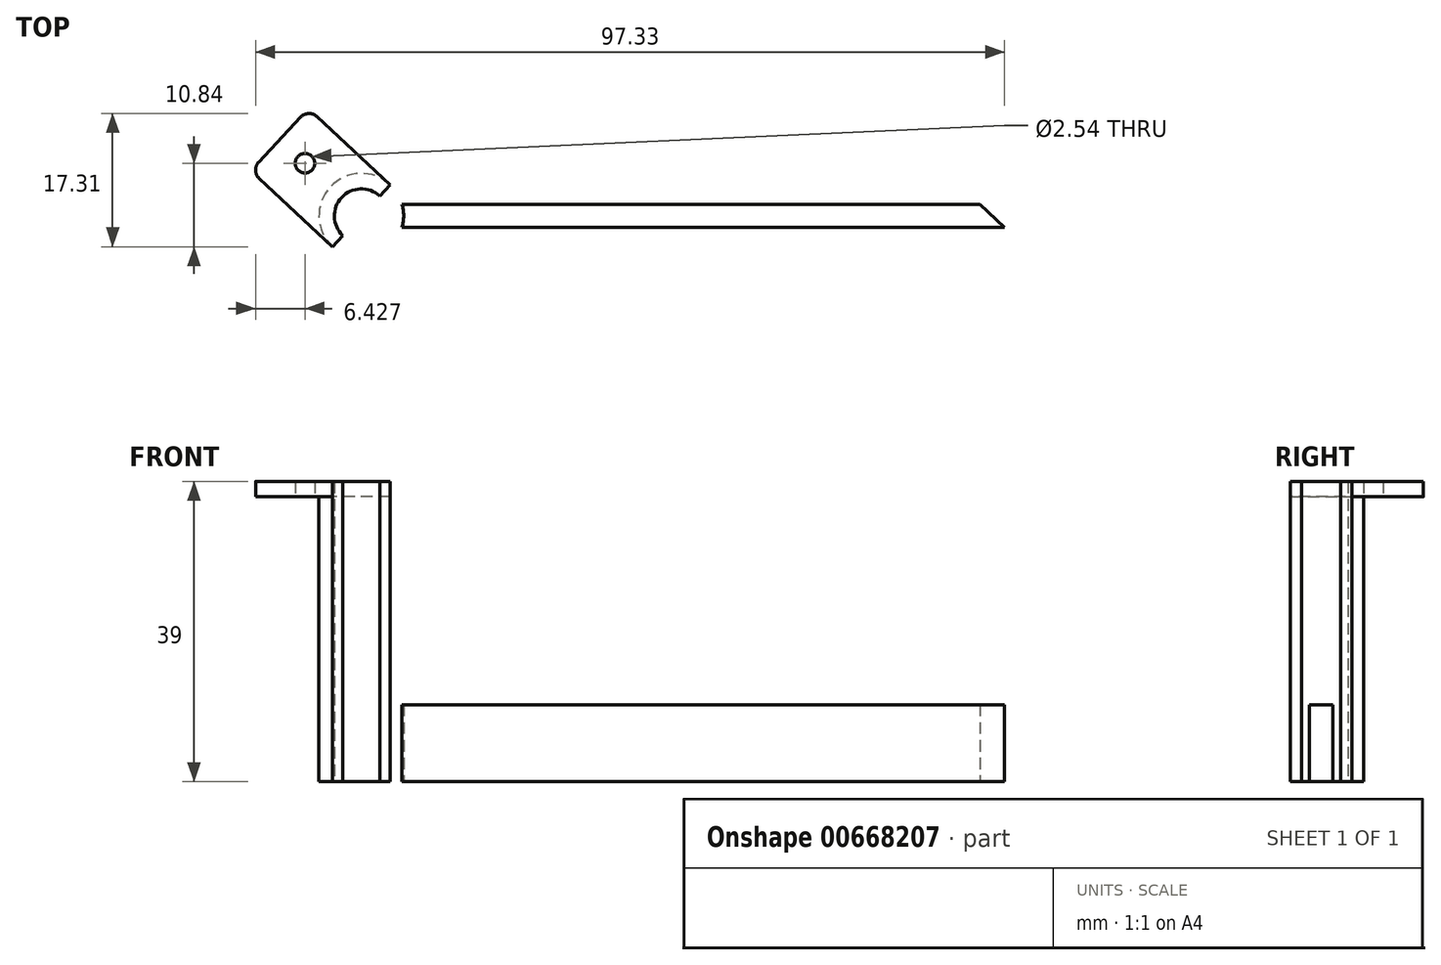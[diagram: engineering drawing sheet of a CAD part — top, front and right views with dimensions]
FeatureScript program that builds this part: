
annotation { "Feature Type Name" : "Feature", "Feature Type Description" : "" }
export const myFeature = defineFeature(function(context is Context, id is Id, definition is map)
    precondition{}
    {
        {
            var Q0;
            Q0=qCreatedBy(makeId("Top.planeOp"),FACE);
            var sketch = newSketch(context, id + "F0", { "sketchPlane" : qUnion([Q0])});
            skCircle(sketch, "E0", {"center": v(-44.5, 0) * mm, "radius": 3.5 * mm});
            skCircle(sketch, "E1", {"center": v(-44.5, 0) * mm, "radius": 5.5 * mm});
            skLineSegment(sketch, "E2", {"start": v(-39.2, 1.5) * mm, "end": v(35.87, 1.5) * mm});
            skLineSegment(sketch, "E3.MirrorCS", {"start": v(-39.2, -1.5) * mm, "end": v(39.1, -1.5) * mm});
            skPoint(sketch, "E4.orphan", {"position": v(39.1, -1.5) * mm});
            skLineSegment(sketch, "E5.bottom", {"start": v(-40.75, 4.02) * mm, "end": v(-48.25, -4.02) * mm});
            skLineSegment(sketch, "E5.top", {"start": v(-52.38, 12.81) * mm, "end": v(-57.83, 6.96) * mm});
            skLineSegment(sketch, "E5.left", {"start": v(-40.75, 4.02) * mm, "end": v(-50.26, 12.89) * mm});
            skLineSegment(sketch, "E5.right", {"start": v(-48.25, -4.02) * mm, "end": v(-57.76, 4.84) * mm});
            skPoint(sketch, "E6", {"position": v(-48.25, -4.02) * mm});
            skCircle(sketch, "E7", {"center": v(-51.81, 6.82) * mm, "radius": 1.27 * mm});
            skPoint(sketch, "E8.visualSharp", {"position": v(-58.86, 5.87) * mm});
            skArc(sketch, "E8.filletArc", {"start": v(-57.83, 6.96) * mm, "mid": v(-58.23, 5.89) * mm, "end": v(-57.76, 4.84) * mm});
            skPoint(sketch, "E9.visualSharp", {"position": v(-51.35, 13.91) * mm});
            skArc(sketch, "E9.filletArc", {"start": v(-50.26, 12.89) * mm, "mid": v(-51.33, 13.3) * mm, "end": v(-52.38, 12.81) * mm});
            skLineSegment(sketch, "E10", {"start": v(39.1, -1.5) * mm, "end": v(35.87, 1.5) * mm});
            skPoint(sketch, "E11.orphan", {"position": v(39.1, 1.5) * mm});
            skSolve(sketch);
        }
        {
            var Q0;
            {var subQ0=sQuery(id+"F0.wireOp",EDGE,"E2");Q0=makeQuery(id+"F0.imprint","IMPRINT",FACE,{"disambiguationData":[TD([[makeQuery(id+"F0.imprint","IMPRINT",EDGE,{"derivedFrom":subQ0}),-1.0]])]});}
            extrude(context, id + "F1", {"entities" : qUnion([Q0]), "depth" : 10 * mm});
        }
        {
            var Q0;
            Q0=makeQuery(id+"F0.imprint","IMPRINT",FACE,{"disambiguationData":[TD([[makeQuery(id+"F0.imprint","IMPRINT",EDGE,{"derivedFrom":sQuery(id+"F0.wireOp",EDGE,"E0")}),-1.0]])]});
            var Q1;
            Q1=makeQuery(id+"F0.imprint","IMPRINT",FACE,{"disambiguationData":[TD([[makeQuery(id+"F0.imprint","IMPRINT",EDGE,{"derivedFrom":sQuery(id+"F0.wireOp",EDGE,"d6ee0b0e-3c25-4719-a539-6223edddca480.MirrorC")}),1.0]])]});
            var Q2;
            {var subQ3=sQuery(id+"F0.wireOp",EDGE,"E5.bottom");var subQ6=sQuery(id+"F0.wireOp",EDGE,"E0");var subQ7=makeQuery(id+"F0.imprint","INTERSECT",VERTEX,{"disambiguationData":[OD(0.0)],"derivedFrom":[subQ6,subQ3]});Q2=makeQuery(id+"F0.imprint","IMPRINT",FACE,{"disambiguationData":[TD([[makeQuery(id+"F0.imprint","IMPRINT",EDGE,{"disambiguationData":[TD([[subQ7,1.0]])],"derivedFrom":subQ6}),-1.0]])]});}
            extrude(context, id + "F2", {"entities" : qUnion([Q0, Q1, Q2]), "operationType" : NewBodyOperationType.ADD, "depth" : 39 * mm, "offsetDistance" : 25 * mm});
        }
        {
            var Q0;
            Q0=makeQuery(id+"F0.imprint","IMPRINT",FACE,{"disambiguationData":[TD([[makeQuery(id+"F0.imprint","IMPRINT",EDGE,{"derivedFrom":sQuery(id+"F0.wireOp",EDGE,"E5.top")}),1.0]])]});
            var sketch = newSketch(context, id + "F3", { "sketchPlane" : qUnion([Q0])});
            skSolve(sketch);
        }
        {
            var Q0;
            Q0=makeQuery(id+"F3.imprint","IMPRINT",FACE,{"disambiguationData":[TD([[makeQuery(id+"F3.imprint","IMPRINT",EDGE,{"derivedFrom":makeQuery(id+"F0.imprint","IMPRINT",EDGE,{"derivedFrom":sQuery(id+"F0.wireOp",EDGE,"E5.top")})}),1.0]])]});
            extrude(context, id + "F4", {"entities" : qUnion([Q0]), "operationType" : NewBodyOperationType.ADD, "depth" : 39 * mm, "offsetDistance" : 25 * mm});
        }
        {
            var Q0;
            Q0=makeQuery(id+"F0.imprint","IMPRINT",FACE,{"disambiguationData":[TD([[makeQuery(id+"F0.imprint","IMPRINT",EDGE,{"derivedFrom":sQuery(id+"F0.wireOp",EDGE,"E5.top")}),1.0]])]});
            extrude(context, id + "F5", {"entities" : qUnion([Q0]), "operationType" : NewBodyOperationType.REMOVE, "depth" : 37 * mm, "offsetDistance" : 25 * mm});
        }
    });
